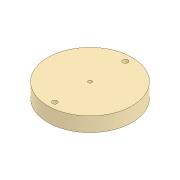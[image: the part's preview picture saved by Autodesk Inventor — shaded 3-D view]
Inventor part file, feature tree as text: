
AUTODESK INVENTOR PART (.ipt)
format: ipt  version: 2020 (Build 240168000, 168)  size: 99,328 bytes
history: native  units: mm
features: extrude x2, sketch x2, other x1, chamfer x1
ambient origin geometry x8: Origin, YZ Plane, XZ Plane, XY Plane, X Axis, Y Axis, Z Axis, Center Point
bodies: Body1 (feature_tree)
feature tree (6):
  other  "Sólido1"
  extrude  "Extrusão1"  Depth=12.0mm TaperAngle=0.0deg
  extrude  "Extrusão2"  Depth=12.0mm
  chamfer  "Chanfro1"  Distance=4.2mm
  sketch  "Esboço1"  dims[d0=69.9mm d1=12.0mm d2=0.0mm]
  sketch  "Esboço2"  dims[d3=3.0mm d4=4.2mm d5=4.2mm d6=12.0mm d7=0.0mm d8=2.5mm d9=2.0mm d10=45.0deg]
